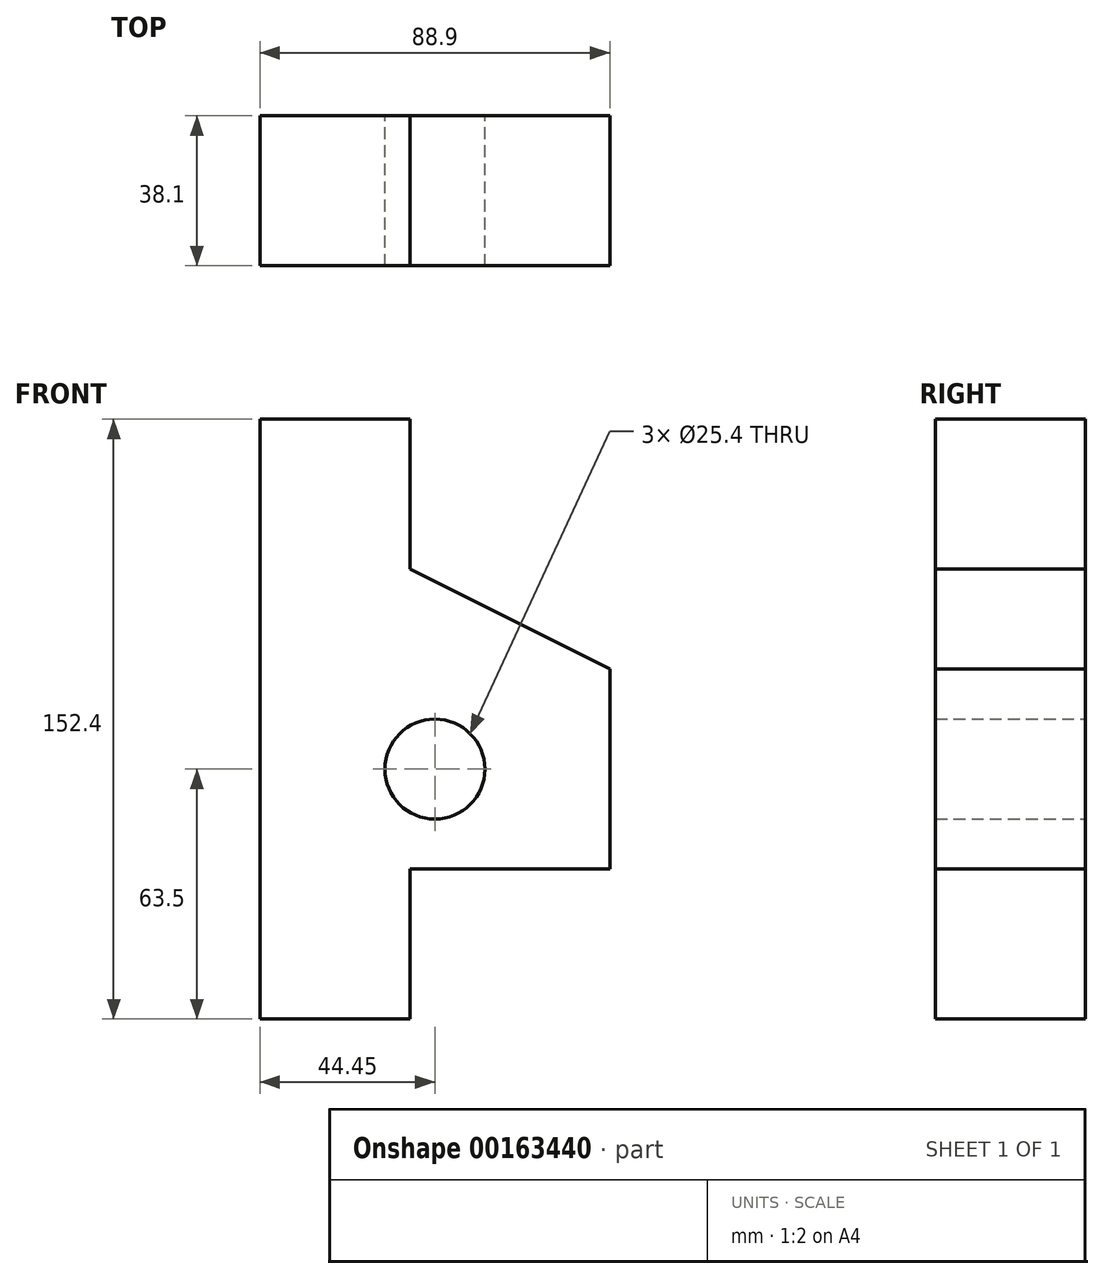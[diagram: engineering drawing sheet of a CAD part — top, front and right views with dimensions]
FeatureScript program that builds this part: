
annotation { "Feature Type Name" : "Feature", "Feature Type Description" : "" }
export const myFeature = defineFeature(function(context is Context, id is Id, definition is map)
    precondition{}
    {
        {
            var Q0;
            Q0=qCreatedBy(makeId("Front.planeOp"),FACE);
            var sketch = newSketch(context, id + "F0", { "sketchPlane" : qUnion([Q0])});
            skLineSegment(sketch, "E0", {"start": v(0, 0) * mm, "end": v(0, 152.4) * mm});
            skLineSegment(sketch, "E1", {"start": v(0, 152.4) * mm, "end": v(38.1, 152.4) * mm});
            skLineSegment(sketch, "E2", {"start": v(88.9, 88.9) * mm, "end": v(88.9, 38.1) * mm});
            skLineSegment(sketch, "E3", {"start": v(88.9, 38.1) * mm, "end": v(38.1, 38.1) * mm});
            skLineSegment(sketch, "E4", {"start": v(38.1, 38.1) * mm, "end": v(38.1, 0) * mm});
            skLineSegment(sketch, "E5", {"start": v(38.1, 0) * mm, "end": v(0, 0) * mm});
            skLineSegment(sketch, "E6", {"start": v(38.1, 152.4) * mm, "end": v(38.1, 114.3) * mm});
            skLineSegment(sketch, "E7", {"start": v(38.1, 114.3) * mm, "end": v(88.9, 88.9) * mm});
            skLineSegment(sketch, "E8", {"start": v(38.1, 114.3) * mm, "end": v(38.1, 38.1) * mm, "construction": true});
            skCircle(sketch, "E9", {"center": v(44.45, 63.5) * mm, "radius": 12.7 * mm});
            skLineSegment(sketch, "E10", {"start": v(88.9, 88.9) * mm, "end": v(0, 88.9) * mm, "construction": true});
            skLineSegment(sketch, "E11", {"start": v(0, 88.9) * mm, "end": v(88.9, 38.1) * mm, "construction": true});
            skSolve(sketch);
        }
        {
            var Q0;
            Q0 = qSketchRegion(id + "F0", true);
            extrude(context, id + "F1", {"entities" : qUnion([Q0]), "depth" : 38.1 * mm});
        }
    });
